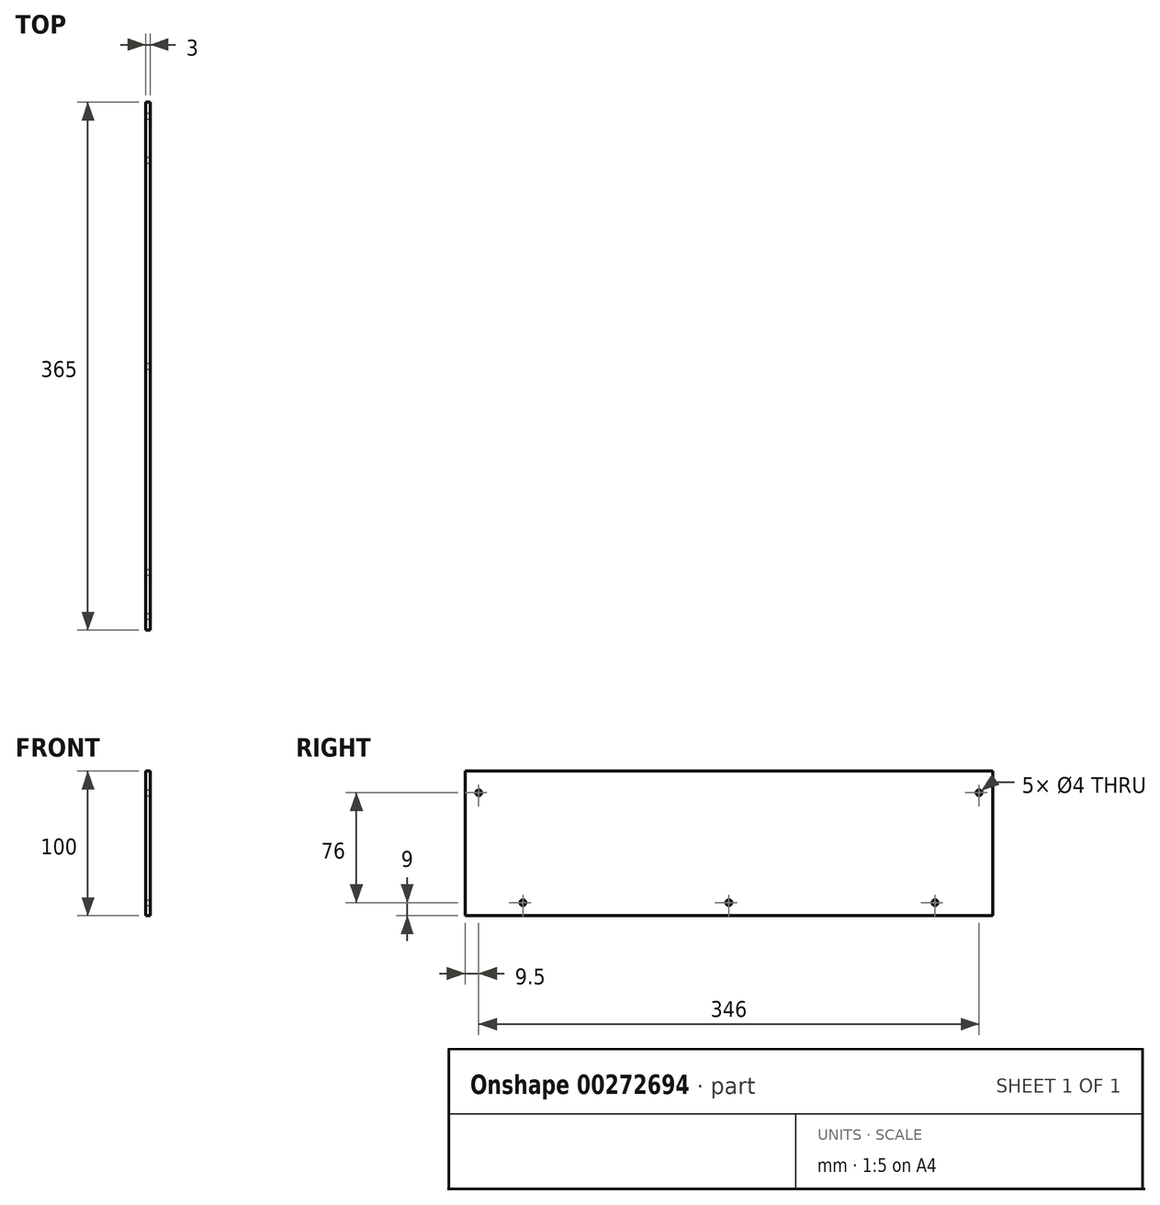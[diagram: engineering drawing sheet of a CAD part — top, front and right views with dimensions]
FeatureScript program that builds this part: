
annotation { "Feature Type Name" : "Feature", "Feature Type Description" : "" }
export const myFeature = defineFeature(function(context is Context, id is Id, definition is map)
    precondition{}
    {
        {
            var Q0;
            Q0=qCreatedBy(makeId("Top.planeOp"),FACE);
            var sketch = newSketch(context, id + "F0", { "sketchPlane" : qUnion([Q0])});
            skLineSegment(sketch, "E0.bottom", {"start": v(0, -182.5) * mm, "end": v(-3, -182.5) * mm});
            skLineSegment(sketch, "E0.top", {"start": v(0, 182.5) * mm, "end": v(-3, 182.5) * mm});
            skLineSegment(sketch, "E0.left", {"start": v(0, -182.5) * mm, "end": v(0, 182.5) * mm});
            skLineSegment(sketch, "E0.right", {"start": v(-3, -182.5) * mm, "end": v(-3, 182.5) * mm});
            skSolve(sketch);
        }
        {
            var Q0;
            Q0=makeQuery(id+"F0.imprint","IMPRINT",FACE,{"disambiguationData":[TD([[makeQuery(id+"F0.imprint","IMPRINT",EDGE,{"derivedFrom":sQuery(id+"F0.wireOp",EDGE,"E0.bottom")}),-1.0]])]});
            extrude(context, id + "F1", {"entities" : qUnion([Q0]), "depth" : 100 * mm});
        }
        {
            var Q0;
            Q0=makeQuery(id+"F1.opExtrude","SWEPT_FACE",FACE,{"disambiguationData":[OSD([sQuery(id+"F0.wireOp",EDGE,"E0.left")])]});
            var sketch = newSketch(context, id + "F2", { "sketchPlane" : qUnion([Q0])});
            skLineSegment(sketch, "E1", {"start": v(0, 0) * mm, "end": v(0, 100) * mm, "construction": true});
            skPoint(sketch, "E2", {"position": v(173, 85) * mm});
            skPoint(sketch, "E3", {"position": v(142.5, 9) * mm});
            skPoint(sketch, "E4.MirrorP", {"position": v(-173, 85) * mm});
            skPoint(sketch, "E5.MirrorP", {"position": v(-142.5, 9) * mm});
            skPoint(sketch, "E6", {"position": v(0, 9) * mm});
            skSolve(sketch);
        }
        {
            var Q0;
            Q0=sQuery(id+"F2.wireOp",VERTEX,"E4.MirrorP");
            var Q1;
            Q1=sQuery(id+"F2.wireOp",VERTEX,"E5.MirrorP");
            var Q2;
            Q2=sQuery(id+"F2.wireOp",VERTEX,"E6");
            var Q3;
            Q3=sQuery(id+"F2.wireOp",VERTEX,"E3");
            var Q4;
            Q4=sQuery(id+"F2.wireOp",VERTEX,"E2");
            var Q5;
            Q5=makeQuery(id+"F1.opExtrude","SWEPT_BODY",BODY,{"disambiguationData":[OSD([sQuery(id+"F0.wireOp",EDGE,"E0.bottom"),sQuery(id+"F0.wireOp",EDGE,"E0.top"),sQuery(id+"F0.wireOp",EDGE,"E0.left"),sQuery(id+"F0.wireOp",EDGE,"E0.right")])]});
            hole(context, id + "F3", {"style" : HoleStyle.SIMPLE, "endStyle" : HoleEndStyle.THROUGH, "holeDiameter" : 4 * mm, "majorDiameter" : 5 * mm, "isTappedThrough" : true, "tappedDepth" : 12 * mm, "tapClearance" : 3, "startFromSketch" : true, "locations" : qUnion([Q0, Q1, Q2, Q3, Q4]), "scope" : qUnion([Q5])});
        }
    });
